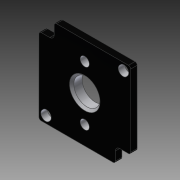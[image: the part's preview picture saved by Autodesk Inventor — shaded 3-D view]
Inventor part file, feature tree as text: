
AUTODESK INVENTOR PART (.ipt)
format: ipt  version: 2014 SP1 (Build 180222100, 222)  size: 262,144 bytes
history: native  units: in
note: dims shown in document units (in); Inventor stores cm internally (conversion verified against a paired STEP export)
features: fillet x1, other x1, imported_body x1
ambient origin geometry x8: Origin, YZ Plane, XZ Plane, XY Plane, X Axis, Y Axis, Z Axis, Center Point
bodies: Body1 (feature_tree)
feature tree (3):
  fillet  "Fillet4"  [1 undecoded]
  other  "217-2822-003 Rev4.ipt1"
  imported_body  "Base1"
note: 1 required parameter value undecoded (feature->parameter linkage not recoverable at this tier; creation-order binding heuristic only, values carry confidence <= 0.55)
